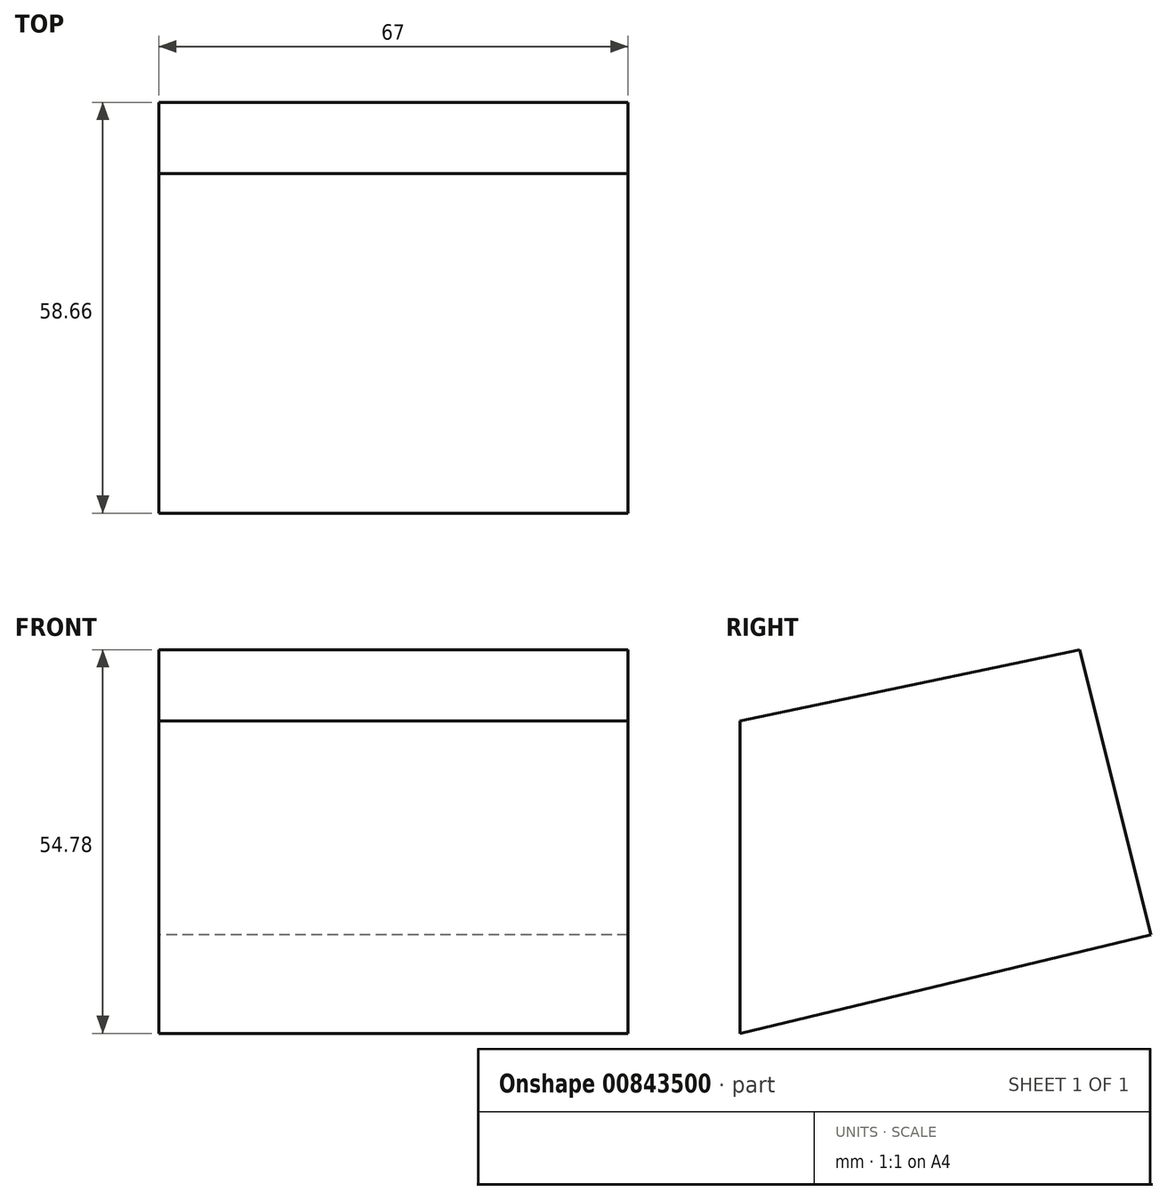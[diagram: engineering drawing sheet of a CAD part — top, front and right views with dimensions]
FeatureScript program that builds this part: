
annotation { "Feature Type Name" : "Feature", "Feature Type Description" : "" }
export const myFeature = defineFeature(function(context is Context, id is Id, definition is map)
    precondition{}
    {
        {
            var Q0;
            Q0=qCreatedBy(makeId("Right.planeOp"),FACE);
            var sketch = newSketch(context, id + "F0", { "sketchPlane" : qUnion([Q0])});
            skLineSegment(sketch, "E0", {"start": v(-45.1, 37.53) * mm, "end": v(-45.1, 3.56) * mm});
            skLineSegment(sketch, "E1", {"start": v(13.56, 17.66) * mm, "end": v(3.4, 58.34) * mm});
            skLineSegment(sketch, "E2", {"start": v(-45.1, 48.17) * mm, "end": v(-45.1, 31.85) * mm});
            skLineSegment(sketch, "E3", {"start": v(-45.1, 31.85) * mm, "end": v(-45.1, 3.56) * mm});
            skLineSegment(sketch, "E4", {"start": v(3.4, 58.34) * mm, "end": v(-45.1, 48.17) * mm});
            skLineSegment(sketch, "E5", {"start": v(-45.1, 48.17) * mm, "end": v(-45.1, 3.56) * mm});
            skLineSegment(sketch, "E6", {"start": v(-45.1, 3.56) * mm, "end": v(13.56, 17.66) * mm});
            skPoint(sketch, "E7.orphan", {"position": v(-45.1, 64.5) * mm});
            skSolve(sketch);
        }
        {
            var Q0;
            Q0=makeQuery(id+"F0.imprint","IMPRINT",FACE,{"disambiguationData":[TD([[makeQuery(id+"F0.imprint","IMPRINT",EDGE,{"derivedFrom":sQuery(id+"F0.wireOp",EDGE,"E1")}),1.0]])]});
            extrude(context, id + "F1", {"entities" : qUnion([Q0]), "depth" : 67 * mm, "offsetDistance" : 25 * mm});
        }
    });
